# Revit family: Fire_Extinguisher
name_source: partatom
category: Generic Models
units: mm (PartAtom-declared; Revit-internal decimal feet)

## family parameters
Always vertical = Yes
Can host rebar = No
Classification Number = 23.65.70.17.27
Cut with Voids When Loaded = No
Host = Wall
Maintain Annotation Orientation = No
Part Type = Normal
Room Calculation Point = No
Round Connector Dimension = Use Diameter
Shared = No

## types (8) — shared parameters
Assembly Code = D4030100
Body = 1' - 6"
BodyHeight = 0' - 0"
Construction Details = http://www.arcat.com
Default Elevation = 0' - 0"
Discharge Agent = Dry Chemical
Expected Lifespan (Years) = 10
Green Building-LEED = http://www.arcat.com
Keynote = 10520.A1
Maintenance Schedule (Months) = 12
Manufacturer = Generic
Manufacturer Fax = (203) 929-2444
Model = Generic
Product Data = http://www.arcat.com
Product Properties = http://www.arcat.com
Radius = 0' - 2"
Specification = http://www.arcat.com
Throat = 0' - 0 5/8"
URL = www.arcat.com
Warranty Duration (Years) = 1

## per-type parameters (varying)
| type | Description | UL Rating |
| 10-A,80-BC | 10-A,80-B:C Fire Extinguisher - Dy Chemical | 10-A,80-B:C |
| 1-A,10BC | 1-A,10BC Fire Extinguisher - Dy Chemical | 1-A,10-B:C |
| 2A,10BC | 2-A,10-B:C Fire Extinguisher - Dy Chemical | 2-A,10-B:C |
| 3A,40BC | 3-A,40-B:C Fire Extinguisher - Dy Chemical | 3-A,40-B:C |
| 4A,60BC | 4-A,60-B:C Fire Extinguisher - Dy Chemical | 4-A,60-B:C |
| 10-BC | 10-B:C Fire Extinguisher - Dy Chemical | 10-B:C |
| 60-BC | 60-B:C Fire Extinguisher - Dy Chemical | 60-B:C |
| 80-BC | 80-B:C Fire Extinguisher - Dy Chemical | 80-B:C |

## geometry (parser evidence)
native form markers: Sweep x3
no freeform markers — native parametric forms only
